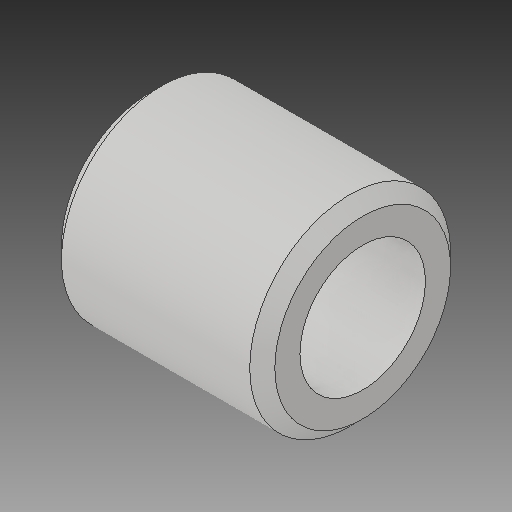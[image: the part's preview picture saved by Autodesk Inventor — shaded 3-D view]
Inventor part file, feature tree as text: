
AUTODESK INVENTOR PART (.ipt)
format: ipt  version: 2017 (Build 210142000, 142)  size: 105,472 bytes
history: native  units: in
note: dims shown in document units (in); Inventor stores cm internally (conversion verified against a paired STEP export)
features: chamfer x1
ambient origin geometry x8: Origin, YZ Plane, XZ Plane, XY Plane, X Axis, Y Axis, Z Axis, Center Point
bodies: Solid1 (feature_tree)
feature tree (1):
  chamfer  "Chamfer1"  [1 undecoded]
note: 1 required parameter value undecoded (feature->parameter linkage not recoverable at this tier; creation-order binding heuristic only, values carry confidence <= 0.55)
